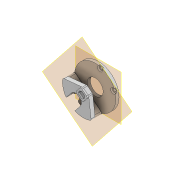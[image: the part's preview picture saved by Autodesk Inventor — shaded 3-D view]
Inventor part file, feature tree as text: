
AUTODESK INVENTOR PART (.ipt)
format: ipt  version: 2022 (Build 260153000, 153)  size: 452,608 bytes
history: native  units: in
note: dims shown in document units (in); Inventor stores cm internally (conversion verified against a paired STEP export)
features: sketch x9, extrude x8, projected_geometry x6, reference x5, other x4, plane x2, fillet x2, hole x1
ambient origin geometry x8: Origin, YZ Plane, XZ Plane, XY Plane, X Axis, Y Axis, Z Axis, Center Point
bodies: Solid1 (feature_tree), Volumenkörper2 (feature_tree)
feature tree (37):
  plane  "Work Plane1"
  extrude  "Extrusion1"  Depth=0.0787in
  hole  "Bohrung1"  [1 undecoded]
  extrude  "Extrusion4"  Depth=0.0787in
  plane  "Arbeitsebene2"
  extrude  "Extrusion6"  Depth=0.2756in TaperAngle=0.0deg
  fillet  "Rundung1"  Radius=0.2651in
  extrude  "Extrusion8"  Depth=0.0787in
  fillet  "Rundung2"  Radius=0.1969in
  extrude  "Extrusion9"  Depth=0.3543in TaperAngle=0.0deg
  extrude  "Extrusion10"  Depth=0.0787in
  extrude  "Extrusion11"  TaperAngle=0.0deg  [1 undecoded]
  extrude  "Extrusion12"  TaperAngle=0.0deg  [1 undecoded]
  sketch  "Sketch1"  dims[d0=0.1575in d1=0.0in]
  reference  "Reference1"
  reference  "Reference5"
  reference  "Reference6"
  reference  "Reference7"
  sketch  "Skizze4"  dims[d9=0.126in d10=0.75in d11=0.2559in d12=0.0787in d13=0.5635in d14=1.0in d15=0.8108in d17=0.7874in]
  reference  "Referenz9"
  sketch  "Skizze6"  dims[d18=0.5118in d19=0.3937in d20=0.0in]
  sketch  "Skizze10"  dims[d33=0.2756in d34=0.0in d37=0.0787in]
  sketch  "Skizze12"  dims[d40=0.5118in d41=0.2756in d42=0.0in d47=0.2651in]
  sketch  "Skizze14"  dims[d48=0.0197in d49=0.0787in d50=0.1969in d51=0.0in]
  projected_geometry  "Projizierte Kontur5"
  projected_geometry  "Projizierte Kontur6"
  projected_geometry  "Projizierte Kontur7"
  sketch  "Skizze16"  dims[d52=0.0in d53=0.3543in d54=0.0in]
  projected_geometry  "Projizierte Kontur8"
  sketch  "Skizze17"  dims[d55=90.0deg d56=0.0787in]
  projected_geometry  "Projizierte Kontur9"
  sketch  "Skizze18"  dims[d57=1.0236in d58=0.0in d59=0.0in d60=0.0in d61=0.0in]
  projected_geometry  "Projizierte Kontur10"
  other  "<userpath>\Documents\Matchboxscope\INVENTOR\Matchboxscope_v1.iam"
  other  "Matchboxscope_v1.iam"
  other  "Matchboxscope_middle2_v1:1"
  other  "Matchboxscope_middle2_v2:1"
note: 3 required parameter values undecoded (feature->parameter linkage not recoverable at this tier; creation-order binding heuristic only, values carry confidence <= 0.55)
